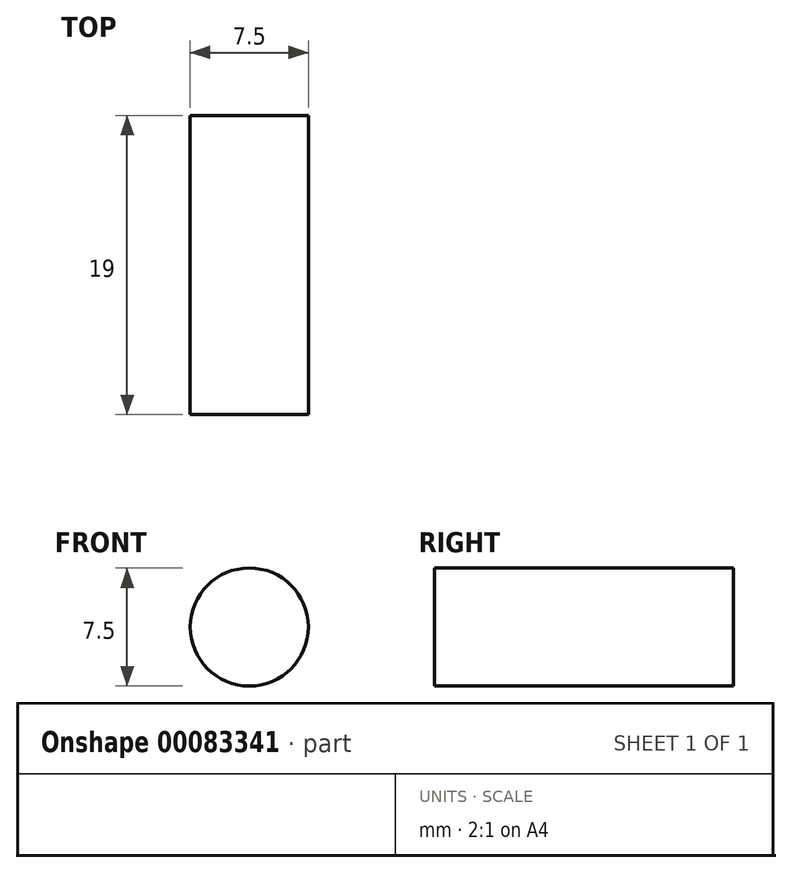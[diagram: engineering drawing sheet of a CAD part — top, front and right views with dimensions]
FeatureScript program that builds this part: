
annotation { "Feature Type Name" : "Feature", "Feature Type Description" : "" }
export const myFeature = defineFeature(function(context is Context, id is Id, definition is map)
    precondition{}
    {
        {
            var Q0;
            Q0=qCreatedBy(makeId("Front.planeOp"),FACE);
            var sketch = newSketch(context, id + "F0", { "sketchPlane" : qUnion([Q0])});
            skCircle(sketch, "E0", {"center": v(0, 0) * mm, "radius": 3.75 * mm});
            skSolve(sketch);
        }
        {
            var Q0;
            Q0 = qSketchRegion(id + "F0", true);
            extrude(context, id + "F1", {"entities" : qUnion([Q0]), "oppositeDirection" : true, "depth" : 19 * mm});
        }
    });
